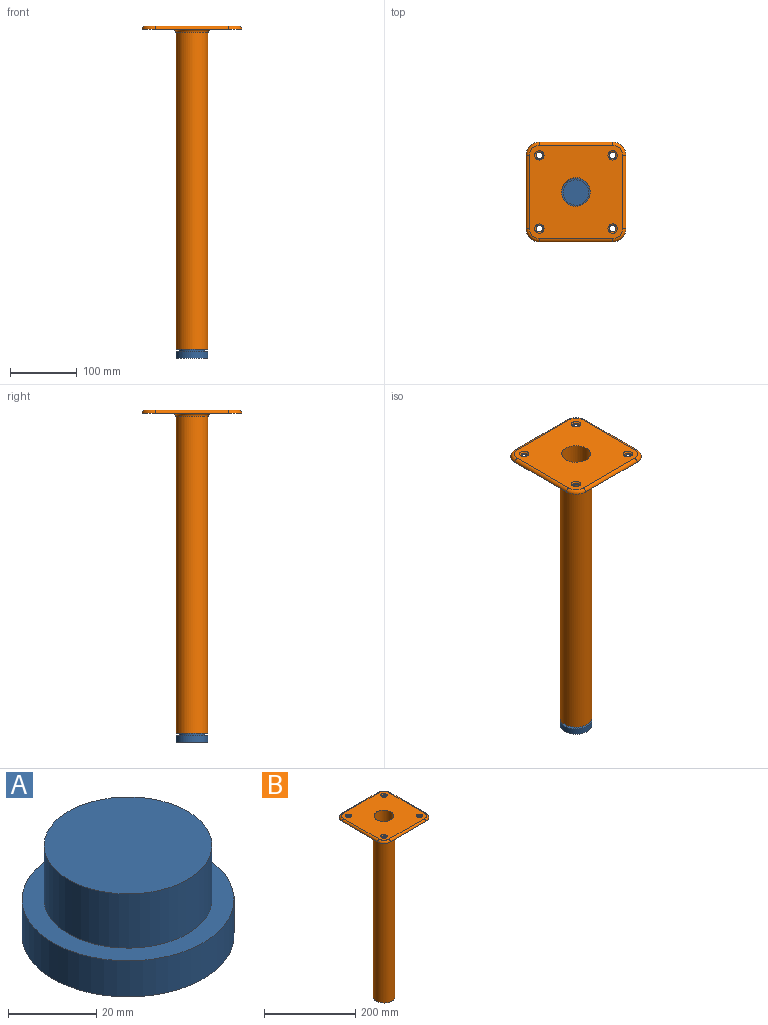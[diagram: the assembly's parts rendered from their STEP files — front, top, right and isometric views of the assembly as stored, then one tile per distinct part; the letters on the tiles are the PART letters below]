
ASSEMBLY  parts=2 mates=1
PART A: 5 faces, bbox 48x48x25 mm
  f0: cylinder r=19mm len=38mm, axis (0,0,-1), area 1790.7mm2, adj f1,f3
  f1: plane 38x38mm, normal (0,0,1), area 1134.1mm2, adj f0
  f2: cylinder r=24mm len=48mm, axis (0,0,-1), area 1508mm2, adj f3,f4
  f3: plane 48x48mm, normal (0,0,1), area 675.4mm2, adj f0,f2
  f4: plane 48x48mm, normal (0,0,-1), area 1809.6mm2, adj f2
PART B: 22 faces, bbox 153.3x153.3x485 mm
  f0: cylinder r=5mm len=10mm, axis (0,0,-1), area 94.2mm2, adj f6,f20
  f1: cylinder r=5mm len=10mm, axis (0,0,-1), area 94.2mm2, adj f6,f19
  f2: cylinder r=5mm len=10mm, axis (0,0,-1), area 94.2mm2, adj f6,f18
  f3: cylinder r=5mm len=10mm, axis (0,0,-1), area 94.2mm2, adj f6,f17
  f4: cylinder r=21.5mm len=485mm, axis (0,0,-1), area 65517.9mm2, adj f5,f8
  f5: plane 140x140mm, normal (0,0,1), area 17338.9mm2, adj f4,f9,f10,f11,f12,f13,f14,f15
  f6: plane 150x150mm, normal (0,0,-1), area 19200.4mm2, adj f0,f1,f2,f3,f9,f10,f11,f12
  f7: cylinder r=24mm len=475mm, axis (0,0,1), area 71628.3mm2, adj f8,f21
  f8: plane 48x48mm, normal (0,0,-1), area 357.4mm2, adj f4,f7
  f9: cylinder r=5mm len=110mm, axis (-1,0,0), area 863.9mm2, adj f5,f6,f10,f11
  f10: torus R=15mm, axis (0,0,1), area 224.3mm2, adj f5,f6,f9,f12
  f11: torus R=15mm, axis (0,0,1), area 224.3mm2, adj f5,f6,f9,f13
  f12: cylinder r=5mm len=110mm, axis (0,1,0), area 863.9mm2, adj f5,f6,f10,f14
  f13: cylinder r=5mm len=110mm, axis (0,-1,0), area 863.9mm2, adj f5,f6,f11,f15
  f14: torus R=15mm, axis (0,0,1), area 224.3mm2, adj f5,f6,f12,f16
  f15: torus R=15mm, axis (0,0,1), area 224.3mm2, adj f5,f6,f13,f16
  f16: cylinder r=5mm len=110mm, axis (1,0,0), area 863.9mm2, adj f5,f6,f14,f15
  f17: torus R=7mm, axis (0,0,1), area 113mm2, adj f3,f5
  f18: torus R=7mm, axis (0,0,1), area 113mm2, adj f2,f5
  f19: torus R=7mm, axis (0,0,1), area 113mm2, adj f1,f5
  f20: torus R=7mm, axis (0,0,1), area 113mm2, adj f0,f5
  f21: torus R=29mm, axis (0,0,1), area 1274mm2, adj f6,f7
PLACE A rot(axis=(0,0,1),180deg) t=(22.82,77.82,-300.56)mm
PLACE B t=(22.82,77.82,192.69)mm
MATE slider A.f0 <-> B.f7  axis (0,0,1) through (22.82,77.82,-275.56)mm
